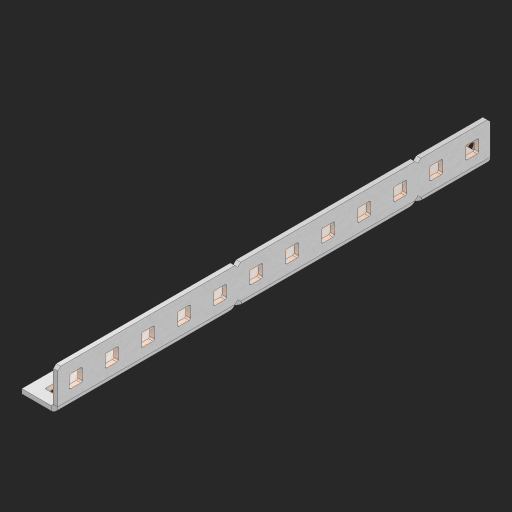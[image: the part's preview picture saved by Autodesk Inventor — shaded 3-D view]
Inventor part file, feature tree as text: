
AUTODESK INVENTOR PART (.ipt)
format: ipt  version: 2023 (Build 270158000, 158)  size: 542,720 bytes
history: native  units: in
note: dims shown in document units (in); Inventor stores cm internally (conversion verified against a paired STEP export)
features: other x29, extrude x23, sheet_metal_op x10, sketch x8, mirror x1, pattern_linear x1, chamfer x1
ambient origin geometry x8: Origin, YZ Plane, XZ Plane, XY Plane, X Axis, Y Axis, Z Axis, Center Point
bodies: Solid1 (feature_tree), Body (feature_tree)
feature tree (73):
  other  "Flange Pattern Plane"
  sheet_metal_op  "Flange Pattern"
  sheet_metal_op  "Body Pattern"
  other  "Arc Length"
  mirror  "Notch Mirror"
  pattern_linear  "Notch Pattern"  Spacing1=0.25in  [1 undecoded]
  chamfer  "End Chamfer"
  extrude  "Half Cut"  Depth=0.0625in
  sketch  "Sketch1"  dims[d0=1.5in]
  other  "Plate1"
  sketch  "Sketch2"  dims[d1=6.0in]
  other  "Plate2"
  sheet_metal_op  "Bend1"
  sheet_metal_op  "Corner1"
  sketch  "Sketch3"  dims[d2=0.0625in]
  other  "Flange Pattern Sketch"
  sketch  "Sketch7"  dims[d3=0.0625in]
  other  "Srf1"
  other  "Srf2"
  sketch  "Sketch8"  dims[d4=0.0312in]
  sketch  "Sketch9"  dims[d5=0.125in]
  other  "Srf91"
  sheet_metal_op  "Body Pattern Sketch"
  other  "Srf92"
  sketch  "Sketch13"  dims[d6=0.0625in]
  sketch  "Sketch14"  dims[d7=0.5in d8=90.0deg d9=0.0312in d10=0.25in d11=0.0625in d12=0.0625in d16=0.182in d17=0.02in d18=0.0625in d19=0.0in d20=0.25in d21=0.25in d46=0.172in d47=1.0in d48=0.0in d49=0.182in d50=0.02in d51=0.25in d52=0.25in d53=0.0625in d54=0.0in d55=0.172in d56=1.0in d57=0.0in d60=4.7244in d62=0.5in d63=0.3937in d65=0.5in d85=0.1473in d86=0.1782in d88=0.04in d89=0.0625in d90=0.0in d91=0.04in d92=0.0491in d95=2.5in d96=0.04in d97=0.25in d98=45.0deg d101=0.0in d102=2.497in d131=0.5in d132=4.7244in d134=0.5in d139=0.5in]
  other  "Srf856"
  other  "Srf1310"
  other  "Srf1311"
  other  "Srf1312"
  other  "Srf1376"
  other  "Srf1377"
  other  "Srf1728"
  other  "Srf1755"
  other  "Srf1878"
  other  "Srf1879"
  other  "Srf1880"
  other  "Srf1881"
  other  "Srf1882"
  other  "Srf1883"
  other  "Srf1942"
  other  "Srf1943"
  other  "Srf1944"
  other  "Srf1945"
  other  "Srf1946"
  other  "Srf1947"
  sheet_metal_op  "Flange Stamp"
  sheet_metal_op  "Flange Circle"
  sheet_metal_op  "Body Stamp"
  sheet_metal_op  "Body Circle"
  sheet_metal_op  "Notch"
  extrude  "ExtrusionSrf2"  Depth=0.0625in
  extrude  "ExtrusionSrf92"  Depth=0.5in
  extrude  "ExtrusionSrf856"  Depth=0.02in
  extrude  "ExtrusionSrf1310"  Depth=0.0625in
  extrude  "ExtrusionSrf1311"  TaperAngle=0.0deg  [1 undecoded]
  extrude  "ExtrusionSrf1312"  Depth=0.5in
  extrude  "ExtrusionSrf1376"  Depth=0.5in
  extrude  "ExtrusionSrf1377"  Depth=0.5in
  extrude  "ExtrusionSrf1728"  Depth=0.5in TaperAngle=0.0deg
  extrude  "ExtrusionSrf1755"  Depth=0.5in
  extrude  "ExtrusionSrf1878"  Depth=0.02in
  extrude  "ExtrusionSrf1879"  Depth=0.5in
  extrude  "ExtrusionSrf1880"  Depth=0.5in
  extrude  "ExtrusionSrf1881"  Depth=0.0625in
  extrude  "ExtrusionSrf1882"  TaperAngle=0.0deg  [1 undecoded]
  extrude  "ExtrusionSrf1883"  Depth=0.5in
  extrude  "ExtrusionSrf1942"  Depth=0.5in TaperAngle=0.0deg
  extrude  "ExtrusionSrf1943"  Depth=0.5in
  extrude  "ExtrusionSrf1944"  Depth=0.5in
  extrude  "ExtrusionSrf1945"  Depth=0.5in
  extrude  "ExtrusionSrf1946"  Depth=0.5in
  extrude  "ExtrusionSrf1947"  Depth=0.5in
note: 3 required parameter values undecoded (feature->parameter linkage not recoverable at this tier; creation-order binding heuristic only, values carry confidence <= 0.55)
